# Revit family: Doors_Security_Troax_Fence-Door_UX-500
name_source: partatom
category: Specialty Equipment
revit_build: Autodesk Revit 2017 (Build: 20190508_0315(x64)
units: mm (PartAtom-declared; Revit-internal decimal feet)

## family parameters
Always vertical = Yes
Cut with Voids When Loaded = No
OmniClass Number = 23.25.40.21.21.11
OmniClass Title = Swinging Gates
Part Type = Normal
Room Calculation Point = No
Round Connector Dimension = Use Diameter
Shared = No
Work Plane-Based = No

## types (1)
- Troax safe UX 500
    AssetType = Fixed
    BIMObjectName = Doors_Security_Troax_Fence-Door_UX-500
    Brand = Troax
    Category = Doors
    Color = Grey
    Constituents = Mesh size: 50x50 mm; tube doorblade 30x20x1,5 mm; wire 5x5 mm, without threshold.
    ConvergoRefNr = 0054-1811-0038-SE
    Cost = 0 $
    Description = The Troax Safe UX500 door is designed to be used togheter with the mesh panel UX 550 system and is suitable for storage areas in need of highest level of protection and is part of a system with specially adapted installation fittings. The System has been tested and approved by the Swedish Theft Prevention Association (SSF) and is used in areas which are particularly susceptible to break-in attempts. The door leaf has a 30x20 mm steel tube frame and two horizontal tubes to create strength and stability. The 50x50 mesh aperture also makes it virtually impossible for a hand to reach through the mesh. Doors are supplied pre-assembled, ready for installation.
    DoorType = Door UX500
    DurationUnit = Year
    Features = The door leaf has a 30x20 mm steel tube frame and two horizontal tubes to create strength and stability. The 50x50 mesh aperture also makes it virtually impossible for a hand to reach through the mesh. Doors are supplied pre-assembled, ready for installation. The door is also equipped with a specially designed cover that provides extra protection to the padlock.
    Finish = Standard colour is grey RAL7037 however other RAL colors or galvanized finish can be offered on request.
    FurniturePanelType = Other
    HasOpening = Yes
    IfcExportAs = IfcSystemFurnitureElementTypePanel
    IfcExportType = DOOR
    MainColor = Grey
    Manufacturer = Troax
    ManufacturerName = Troax
    ManufacturerURL = https://www.troax.com
    Material = Carbon steel
    Model = Troax safe UX 500
    NBSDescription = Metal doorsets
    NBSReference = 45-25-28/344
    Name = Troax_Fence-Door_UX-500
    NominalDepth = 80 mm  [stored 0.262467 ft]
    NominalHeight = 2200 mm
    NominalThickness = 0 mm  [stored 0 ft]
    NominalWidth = 918 mm  [stored 3.01181 ft]
    ProductDatasheet = https://www.troax.com
    ProductInformation = The Troax Safe UX500 door is designed to be used togheter with the mesh panel UX 550 system and is suitable for storage areas in need of highest level of protection and is part of a system with specially adapted installation fittings.
    Revision = 2
    Shape = Sculptured
    Size = 80x2200x918 mm
    URL = https://www.troax.com
    Uniclass2 = Pr_30_59_23_11
    Uniclass2015Description = Carbon steel door frames
    Uniclass2015Reference = Pr_30_59_23_11
    Version = 1
    VersionDate = 01/07/2020
    WallPanelMainMaterial = Steel, Carbon
    WarrantyDurationUnit = Year

note: [stored X ft] marks values corroborated as IEEE doubles in the binary element streams (Revit-internal decimal feet)

## geometry (parser evidence)
native form markers: Sweep x5
no freeform markers — native parametric forms only
